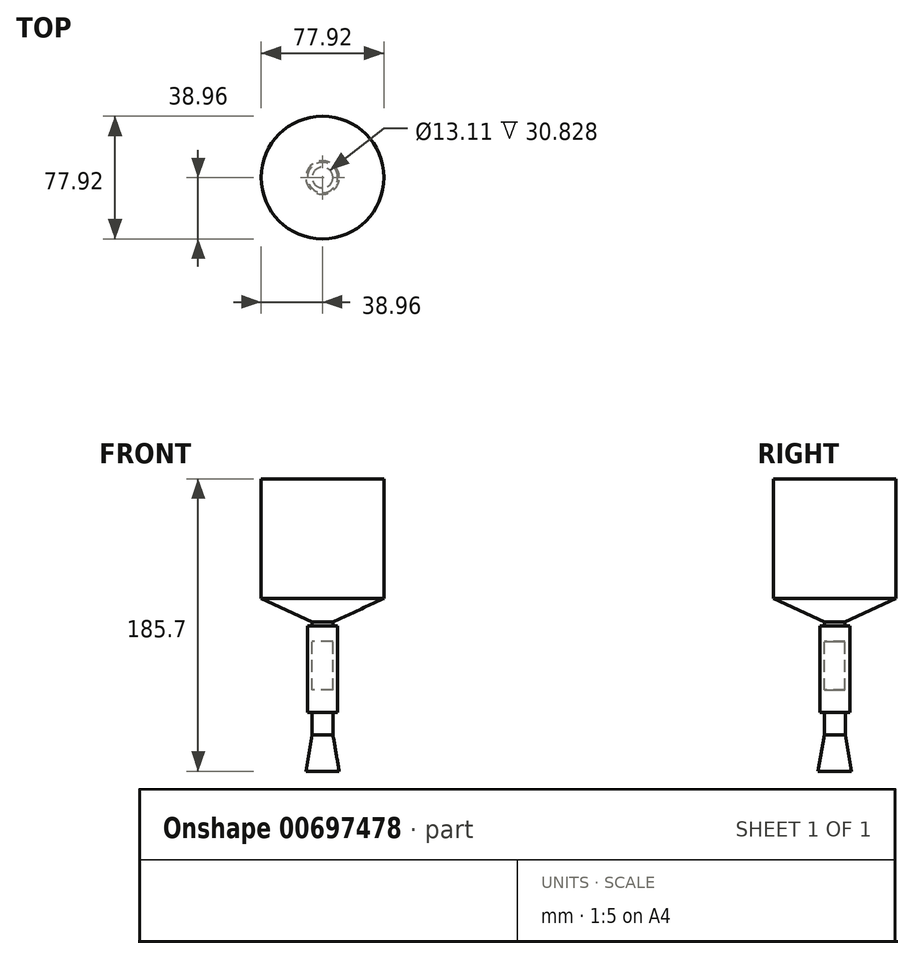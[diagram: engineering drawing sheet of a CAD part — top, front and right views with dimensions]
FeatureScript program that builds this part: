
annotation { "Feature Type Name" : "Feature", "Feature Type Description" : "" }
export const myFeature = defineFeature(function(context is Context, id is Id, definition is map)
    precondition{}
    {
        {
            var Q0;
            Q0=qCreatedBy(makeId("Front.planeOp"),FACE);
            var sketch = newSketch(context, id + "F0", { "sketchPlane" : qUnion([Q0])});
            skLineSegment(sketch, "E0", {"start": v(0, 62.59) * mm, "end": v(38.96, 62.59) * mm});
            skLineSegment(sketch, "E1", {"start": v(38.96, 62.59) * mm, "end": v(38.96, -13.35) * mm});
            skLineSegment(sketch, "E2", {"start": v(38.96, -13.35) * mm, "end": v(0, -13.35) * mm});
            skLineSegment(sketch, "E3", {"start": v(38.96, -13.35) * mm, "end": v(6.56, -28.22) * mm});
            skLineSegment(sketch, "E4", {"start": v(6.56, -28.22) * mm, "end": v(0, -28.22) * mm});
            skLineSegment(sketch, "E5", {"start": v(6.56, -28.22) * mm, "end": v(6.56, -40.67) * mm});
            skLineSegment(sketch, "E6", {"start": v(6.56, -40.67) * mm, "end": v(0, -40.67) * mm});
            skLineSegment(sketch, "E7", {"start": v(6.56, -30.7) * mm, "end": v(9.6, -30.7) * mm});
            skLineSegment(sketch, "E8", {"start": v(9.6, -30.7) * mm, "end": v(9.6, -82.7) * mm});
            skLineSegment(sketch, "E9", {"start": v(9.6, -82.7) * mm, "end": v(6.56, -82.7) * mm});
            skLineSegment(sketch, "E10", {"start": v(6.56, -82.7) * mm, "end": v(6.56, -40.67) * mm});
            skLineSegment(sketch, "E11", {"start": v(0, -71.5) * mm, "end": v(6.56, -71.5) * mm});
            skLineSegment(sketch, "E12", {"start": v(6.56, -71.5) * mm, "end": v(6.56, -82.7) * mm});
            skLineSegment(sketch, "E13", {"start": v(0, -82.7) * mm, "end": v(6.56, -82.7) * mm});
            skLineSegment(sketch, "E14", {"start": v(9.6, -82.7) * mm, "end": v(9.6, -85.64) * mm});
            skLineSegment(sketch, "E15", {"start": v(9.6, -85.64) * mm, "end": v(0, -85.64) * mm});
            skLineSegment(sketch, "E16", {"start": v(6.64, -85.64) * mm, "end": v(6.64, -100.09) * mm});
            skLineSegment(sketch, "E17", {"start": v(6.64, -100.09) * mm, "end": v(0, -100.09) * mm});
            skLineSegment(sketch, "E18", {"start": v(6.64, -100.09) * mm, "end": v(10.58, -123.1) * mm});
            skLineSegment(sketch, "E19", {"start": v(0, -123.1) * mm, "end": v(10.58, -123.1) * mm});
            skLineSegment(sketch, "E20", {"start": v(0, 62.59) * mm, "end": v(0, -140.65) * mm});
            skSolve(sketch);
        }
        {
            var Q0;
            {var subQ0=sQuery(id+"F0.wireOp",EDGE,"E0");Q0=makeQuery(id+"F0.imprint","IMPRINT",FACE,{"disambiguationData":[TD([[makeQuery(id+"F0.imprint","IMPRINT",EDGE,{"derivedFrom":subQ0}),-1.0]])]});}
            var Q1;
            {var subQ0=sQuery(id+"F0.wireOp",EDGE,"E2");Q1=makeQuery(id+"F0.imprint","IMPRINT",FACE,{"disambiguationData":[TD([[makeQuery(id+"F0.imprint","IMPRINT",EDGE,{"derivedFrom":subQ0}),1.0]])]});}
            var Q2;
            {var subQ3=sQuery(id+"F0.wireOp",EDGE,"E4");Q2=makeQuery(id+"F0.imprint","IMPRINT",FACE,{"disambiguationData":[TD([[makeQuery(id+"F0.imprint","IMPRINT",EDGE,{"derivedFrom":subQ3}),1.0]])]});}
            var Q3;
            {var subQ0=sQuery(id+"F0.wireOp",EDGE,"E7");Q3=makeQuery(id+"F0.imprint","IMPRINT",FACE,{"disambiguationData":[TD([[makeQuery(id+"F0.imprint","IMPRINT",EDGE,{"derivedFrom":subQ0}),-1.0]])]});}
            var Q4;
            {var subQ0=sQuery(id+"F0.wireOp",EDGE,"E11");Q4=makeQuery(id+"F0.imprint","IMPRINT",FACE,{"disambiguationData":[TD([[makeQuery(id+"F0.imprint","IMPRINT",EDGE,{"derivedFrom":subQ0}),-1.0]])]});}
            var Q5;
            Q5=makeQuery(id+"F0.imprint","IMPRINT",FACE,{"disambiguationData":[TD([[makeQuery(id+"F0.imprint","IMPRINT",EDGE,{"derivedFrom":sQuery(id+"F0.wireOp",EDGE,"E9")}),1.0]])]});
            var Q6;
            {var subQ3=sQuery(id+"F0.wireOp",EDGE,"E16");Q6=makeQuery(id+"F0.imprint","IMPRINT",FACE,{"disambiguationData":[TD([[makeQuery(id+"F0.imprint","IMPRINT",EDGE,{"derivedFrom":subQ3}),-1.0]])]});}
            var Q7;
            {var subQ0=sQuery(id+"F0.wireOp",EDGE,"E17");Q7=makeQuery(id+"F0.imprint","IMPRINT",FACE,{"disambiguationData":[TD([[makeQuery(id+"F0.imprint","IMPRINT",EDGE,{"derivedFrom":subQ0}),1.0]])]});}
            var Q8;
            Q8=sQuery(id+"F0.wireOp",EDGE,"E20");
            revolve(context, id + "F1", {"entities" : qUnion([Q0, Q1, Q2, Q3, Q4, Q5, Q6, Q7]), "axis" : qUnion([Q8]), "revolveType" : RevolveType.FULL});
        }
        {
            var Q0;
            Q0=makeQuery(id+"F1.opRevolve","SWEPT_BODY",BODY,{"disambiguationData":[OSD([sQuery(id+"F0.wireOp",EDGE,"E0"),sQuery(id+"F0.wireOp",EDGE,"E1"),sQuery(id+"F0.wireOp",EDGE,"E3"),sQuery(id+"F0.wireOp",EDGE,"E5"),sQuery(id+"F0.wireOp",EDGE,"E6"),sQuery(id+"F0.wireOp",EDGE,"E7"),sQuery(id+"F0.wireOp",EDGE,"E8"),sQuery(id+"F0.wireOp",EDGE,"E10"),sQuery(id+"F0.wireOp",EDGE,"E11"),sQuery(id+"F0.wireOp",EDGE,"E14"),sQuery(id+"F0.wireOp",EDGE,"E15"),sQuery(id+"F0.wireOp",EDGE,"E16"),sQuery(id+"F0.wireOp",EDGE,"E18"),sQuery(id+"F0.wireOp",EDGE,"E19"),sQuery(id+"F0.wireOp",EDGE,"E20")])]});
            transform(context, id + "F2", {"entities" : qUnion([Q0]), "transformType" : TransformType.TRANSLATION_3D, "dx" : 0 * mm, "dy" : 254 * mm, "dz" : 0 * mm, "makeCopy" : false});
        }
    });
